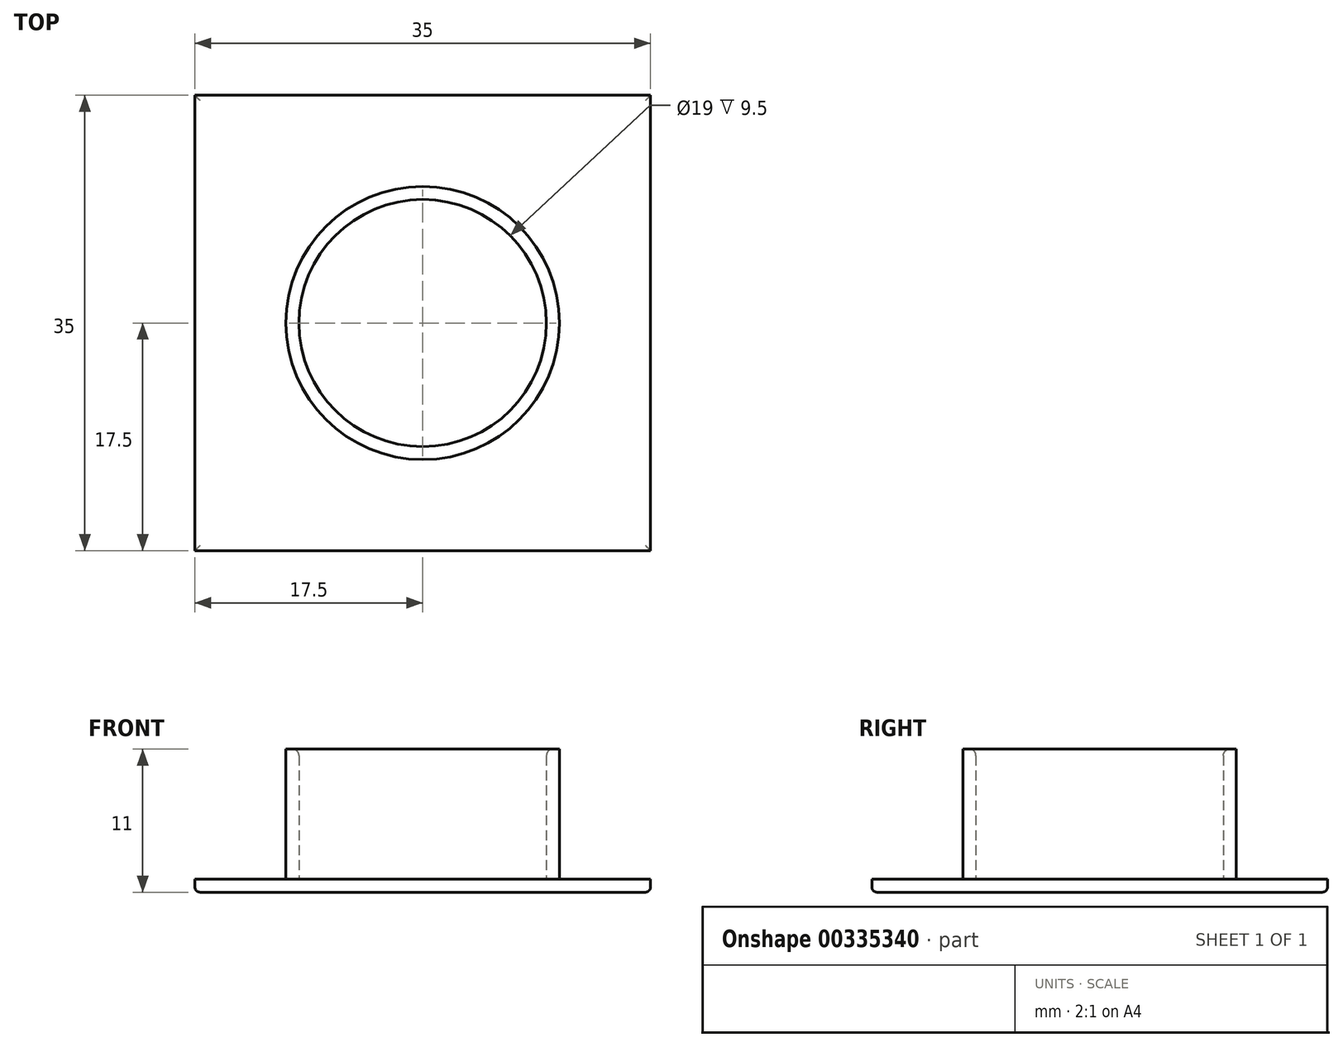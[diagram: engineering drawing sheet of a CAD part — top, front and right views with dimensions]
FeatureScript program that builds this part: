
annotation { "Feature Type Name" : "Feature", "Feature Type Description" : "" }
export const myFeature = defineFeature(function(context is Context, id is Id, definition is map)
    precondition{}
    {
        {
            var Q0;
            Q0=qCreatedBy(makeId("Top.planeOp"),FACE);
            var sketch = newSketch(context, id + "F0", { "sketchPlane" : qUnion([Q0])});
            skLineSegment(sketch, "E0.bottom", {"start": v(17.5, 17.5) * mm, "end": v(-17.5, 17.5) * mm});
            skLineSegment(sketch, "E0.top", {"start": v(17.5, -17.5) * mm, "end": v(-17.5, -17.5) * mm});
            skLineSegment(sketch, "E0.left", {"start": v(17.5, 17.5) * mm, "end": v(17.5, -17.5) * mm});
            skLineSegment(sketch, "E0.right", {"start": v(-17.5, 17.5) * mm, "end": v(-17.5, -17.5) * mm});
            skPoint(sketch, "E0.middle", {"position": v(0, 0) * mm});
            skCircle(sketch, "E1", {"center": v(0, 0) * mm, "radius": 10.5 * mm});
            skCircle(sketch, "E2", {"center": v(0, 0) * mm, "radius": 9.5 * mm});
            skPoint(sketch, "E3", {"position": v(9.5, 0) * mm});
            skPoint(sketch, "E4", {"position": v(10.5, 0) * mm});
            skSolve(sketch);
        }
        {
            var Q0;
            Q0=makeQuery(id+"F0.imprint","IMPRINT",FACE,{"disambiguationData":[TD([[makeQuery(id+"F0.imprint","IMPRINT",EDGE,{"derivedFrom":sQuery(id+"F0.wireOp",EDGE,"E1")}),1.0]])]});
            extrude(context, id + "F1", {"entities" : qUnion([Q0]), "depth" : 10 * mm});
        }
        {
            var Q0;
            Q0=makeQuery(id+"F0.imprint","IMPRINT",FACE,{"disambiguationData":[TD([[makeQuery(id+"F0.imprint","IMPRINT",EDGE,{"derivedFrom":sQuery(id+"F0.wireOp",EDGE,"E1")}),1.0]])]});
            var Q1;
            Q1=makeQuery(id+"F0.imprint","IMPRINT",FACE,{"disambiguationData":[TD([[makeQuery(id+"F0.imprint","IMPRINT",EDGE,{"derivedFrom":sQuery(id+"F0.wireOp",EDGE,"E0.bottom")}),1.0]])]});
            var Q2;
            Q2=makeQuery(id+"F0.imprint","IMPRINT",FACE,{"disambiguationData":[TD([[makeQuery(id+"F0.imprint","IMPRINT",EDGE,{"derivedFrom":sQuery(id+"F0.wireOp",EDGE,"E2")}),1.0]])]});
            extrude(context, id + "F2", {"entities" : qUnion([Q0, Q1, Q2]), "operationType" : NewBodyOperationType.ADD, "oppositeDirection" : true, "depth" : 1 * mm});
        }
        {
            var Q0;
            Q0=makeQuery(id+"F2.opExtrude","CAP_EDGE",EDGE,{"disambiguationData":[OSD([sQuery(id+"F0.wireOp",EDGE,"E0.right")])],"isStart":false});
            var Q1;
            Q1=makeQuery(id+"F2.opExtrude","CAP_EDGE",EDGE,{"disambiguationData":[OSD([sQuery(id+"F0.wireOp",EDGE,"E0.bottom")])],"isStart":false});
            var Q2;
            Q2=makeQuery(id+"F2.opExtrude","CAP_EDGE",EDGE,{"disambiguationData":[OSD([sQuery(id+"F0.wireOp",EDGE,"E0.left")])],"isStart":false});
            var Q3;
            Q3=makeQuery(id+"F2.opExtrude","CAP_EDGE",EDGE,{"disambiguationData":[OSD([sQuery(id+"F0.wireOp",EDGE,"E0.top")])],"isStart":false});
            fillet(context, id + "F3", {"entities" : qUnion([Q0, Q1, Q2, Q3]), "radius" : .4 * mm, "tangentPropagation" : true, "allowEdgeOverflow" : false});
        }
        {
            var Q0;
            Q0=makeQuery(id+"F1.opExtrude","CAP_EDGE",EDGE,{"disambiguationData":[OSD([sQuery(id+"F0.wireOp",EDGE,"E2")])],"isStart":false});
            fillet(context, id + "F4", {"entities" : qUnion([Q0]), "radius" : .5 * mm, "tangentPropagation" : true, "allowEdgeOverflow" : false});
        }
    });
